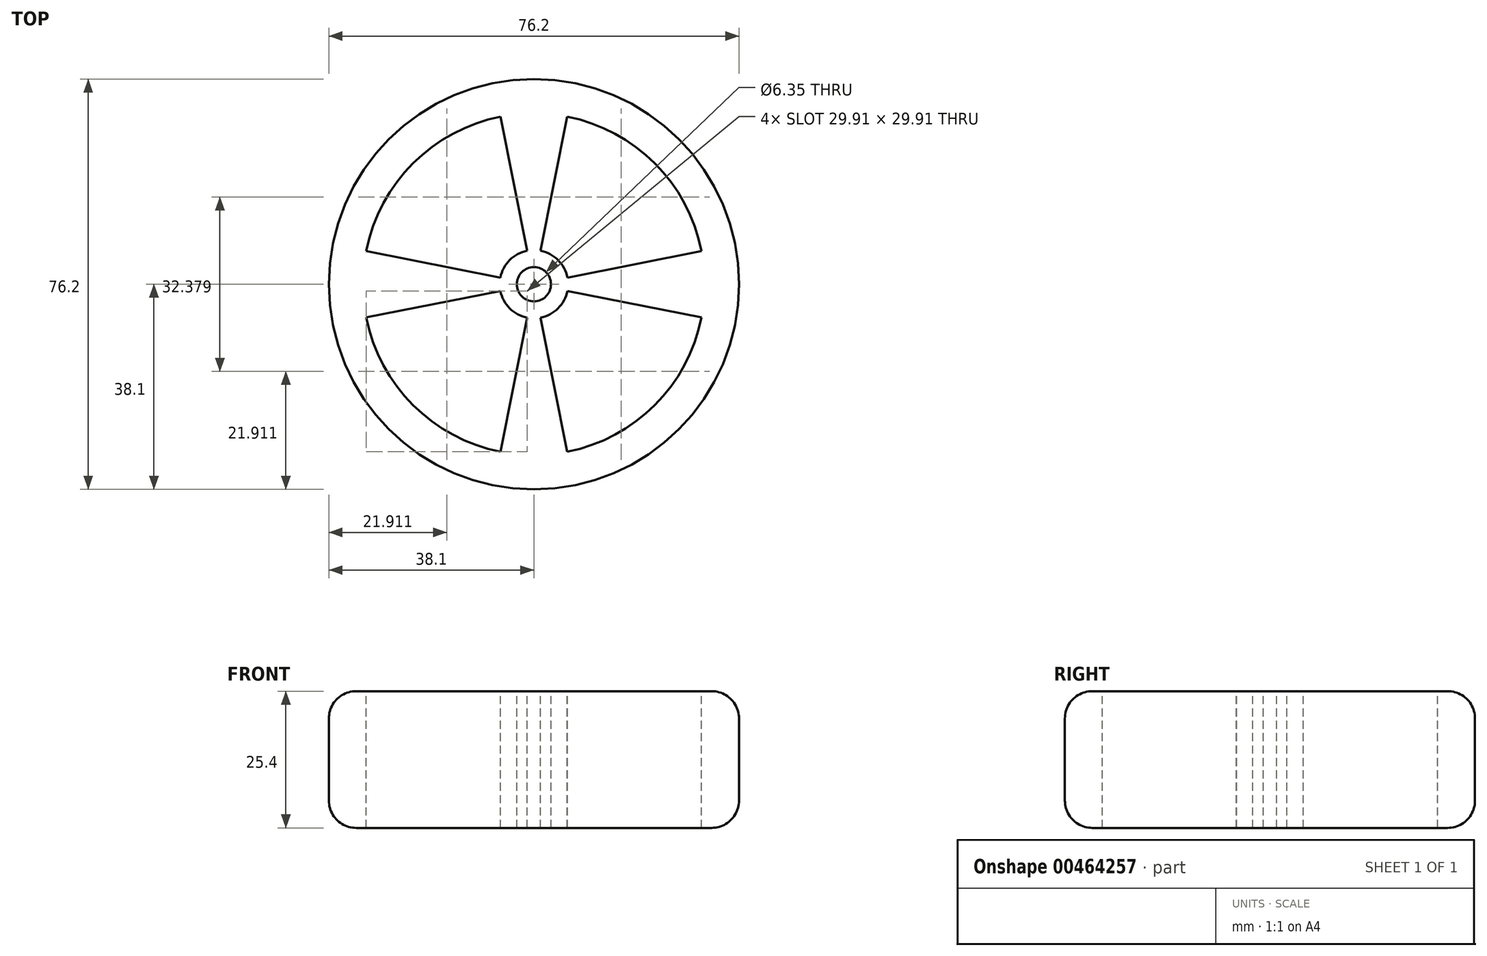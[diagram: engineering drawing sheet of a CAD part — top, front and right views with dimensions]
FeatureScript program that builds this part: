
annotation { "Feature Type Name" : "Feature", "Feature Type Description" : "" }
export const myFeature = defineFeature(function(context is Context, id is Id, definition is map)
    precondition{}
    {
        {
            var Q0;
            Q0=qCreatedBy(makeId("Top.planeOp"),FACE);
            var sketch = newSketch(context, id + "F0", { "sketchPlane" : qUnion([Q0])});
            skCircle(sketch, "E0", {"center": v(0, 0) * mm, "radius": 38.1 * mm});
            skArc(sketch, "E1", {"start": v(-6.18, 31.14) * mm, "mid": v(-22.45, 22.45) * mm, "end": v(-31.14, 6.18) * mm});
            skArc(sketch, "E2", {"start": v(-1.24, 6.23) * mm, "mid": v(-4.5, 4.5) * mm, "end": v(-6.23, 1.24) * mm});
            skCircle(sketch, "E3", {"center": v(0, 0) * mm, "radius": 3.18 * mm});
            skLineSegment(sketch, "E4", {"start": v(-6.18, 31.14) * mm, "end": v(-1.24, 6.23) * mm});
            skArc(sketch, "E5.trimOffspring", {"start": v(-31.14, -6.18) * mm, "mid": v(-22.45, -22.45) * mm, "end": v(-6.18, -31.14) * mm});
            skArc(sketch, "E6.trimOffspring", {"start": v(6.18, -31.14) * mm, "mid": v(22.45, -22.45) * mm, "end": v(31.14, -6.18) * mm});
            skArc(sketch, "E7.trimOffspring", {"start": v(31.14, 6.18) * mm, "mid": v(22.45, 22.45) * mm, "end": v(6.18, 31.14) * mm});
            skLineSegment(sketch, "E8.trimOffspring", {"start": v(-6.23, -1.24) * mm, "end": v(-31.14, -6.18) * mm});
            skLineSegment(sketch, "E9.trimOffspring", {"start": v(-6.23, 1.24) * mm, "end": v(-31.14, 6.18) * mm});
            skLineSegment(sketch, "E10.trimOffspring", {"start": v(1.24, 6.23) * mm, "end": v(6.18, 31.14) * mm});
            skLineSegment(sketch, "E11.trimOffspring", {"start": v(6.23, 1.24) * mm, "end": v(31.14, 6.18) * mm});
            skLineSegment(sketch, "E12.trimOffspring", {"start": v(6.23, -1.24) * mm, "end": v(31.14, -6.18) * mm});
            skLineSegment(sketch, "E13.trimOffspring", {"start": v(1.24, -6.23) * mm, "end": v(6.18, -31.14) * mm});
            skLineSegment(sketch, "E14.trimOffspring", {"start": v(-1.24, -6.23) * mm, "end": v(-6.18, -31.14) * mm});
            skArc(sketch, "E15.trimOffspring", {"start": v(-6.23, -1.24) * mm, "mid": v(-4.5, -4.5) * mm, "end": v(-1.24, -6.23) * mm});
            skArc(sketch, "E16.trimOffspring", {"start": v(1.24, -6.23) * mm, "mid": v(4.5, -4.5) * mm, "end": v(6.23, -1.24) * mm});
            skArc(sketch, "E17.trimOffspring", {"start": v(6.23, 1.24) * mm, "mid": v(4.5, 4.5) * mm, "end": v(1.24, 6.23) * mm});
            skSolve(sketch);
        }
        {
            var Q0;
            Q0 = qSketchRegion(id + "F0", true);
            extrude(context, id + "F1", {"entities" : qUnion([Q0]), "oppositeDirection" : true, "depth" : 25.4 * mm});
        }
        {
            var Q0;
            Q0=makeQuery(id+"F1.opExtrude","SWEPT_FACE",FACE,{"disambiguationData":[OSD([sQuery(id+"F0.wireOp",EDGE,"E0")])]});
            fillet(context, id + "F2", {"entities" : qUnion([Q0]), "radius" : 5.08 * mm, "tangentPropagation" : true, "allowEdgeOverflow" : false});
        }
    });
